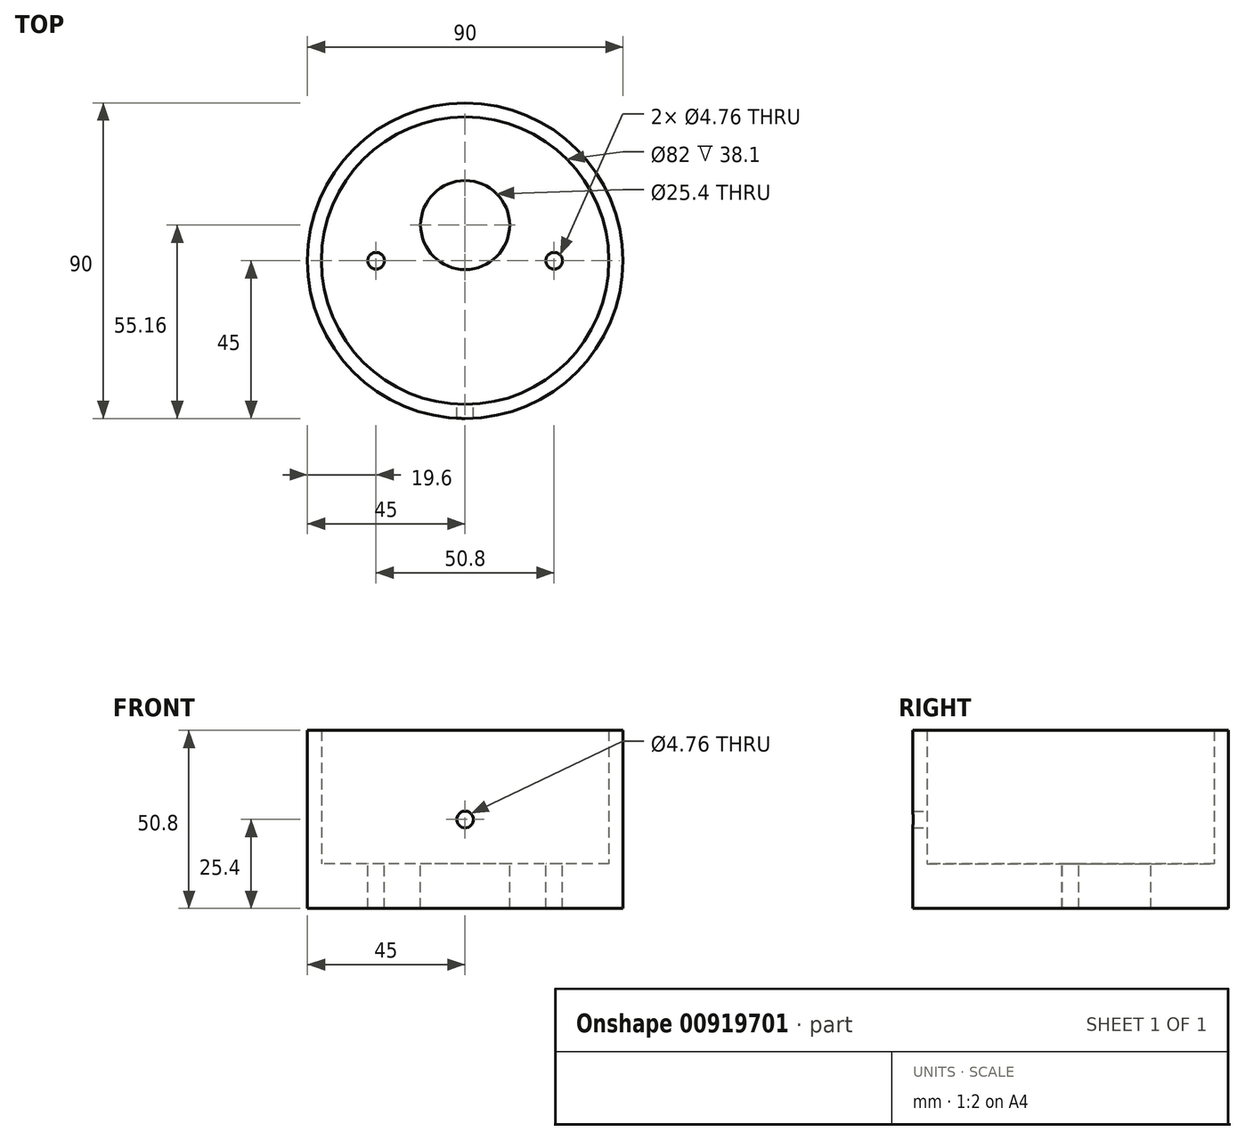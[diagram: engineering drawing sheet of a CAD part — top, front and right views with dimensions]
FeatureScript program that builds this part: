
annotation { "Feature Type Name" : "Feature", "Feature Type Description" : "" }
export const myFeature = defineFeature(function(context is Context, id is Id, definition is map)
    precondition{}
    {
        {
            var Q0;
            Q0=qCreatedBy(makeId("Top.planeOp"),FACE);
            var sketch = newSketch(context, id + "F0", { "sketchPlane" : qUnion([Q0])});
            skCircle(sketch, "E0", {"center": v(0, 0) * mm, "radius": 45 * mm});
            skSolve(sketch);
        }
        {
            var Q0;
            Q0 = qSketchRegion(id + "F0", true);
            extrude(context, id + "F1", {"entities" : qUnion([Q0]), "depth" : 12.7 * mm, "offsetDistance" : 25.4 * mm});
        }
        {
            var Q0;
            Q0=makeQuery(id+"F1.opExtrude","CAP_FACE",FACE,{"disambiguationData":[OSD([sQuery(id+"F0.wireOp",EDGE,"E0")])],"isStart":false});
            var sketch = newSketch(context, id + "F2", { "sketchPlane" : qUnion([Q0])});
            skCircle(sketch, "E1.0", {"center": v(0, 0) * mm, "radius": 45 * mm});
            skCircle(sketch, "E2", {"center": v(0, 0) * mm, "radius": 41 * mm});
            skSolve(sketch);
        }
        {
            var Q0;
            Q0 = qSketchRegion(id + "F2", true);
            extrude(context, id + "F3", {"entities" : qUnion([Q0]), "operationType" : NewBodyOperationType.ADD, "depth" : 38.1 * mm, "offsetDistance" : 25.4 * mm});
        }
        {
            var Q0;
            Q0=qCreatedBy(makeId("Front.planeOp"),FACE);
            var sketch = newSketch(context, id + "F4", { "sketchPlane" : qUnion([Q0])});
            skCircle(sketch, "E3", {"center": v(0, 25.4) * mm, "radius": 2.38 * mm});
            skSolve(sketch);
        }
        {
            var Q0;
            Q0 = qSketchRegion(id + "F4", true);
            extrude(context, id + "F5", {"entities" : qUnion([Q0]), "operationType" : NewBodyOperationType.REMOVE, "depth" : 79.5 * mm, "offsetDistance" : 25.4 * mm});
        }
        {
            var Q0;
            Q0=makeQuery(id+"F1.opExtrude","CAP_FACE",FACE,{"disambiguationData":[OSD([sQuery(id+"F0.wireOp",EDGE,"E0")])],"isStart":false});
            var sketch = newSketch(context, id + "F6", { "sketchPlane" : qUnion([Q0])});
            skCircle(sketch, "E4", {"center": v(-25.4, 0) * mm, "radius": 2.38 * mm});
            skCircle(sketch, "E5", {"center": v(25.4, 0) * mm, "radius": 2.38 * mm});
            skLineSegment(sketch, "E6", {"start": v(-25.4, 0) * mm, "end": v(25.4, 0) * mm, "construction": true});
            skSolve(sketch);
        }
        {
            var Q0;
            Q0 = qSketchRegion(id + "F6", true);
            extrude(context, id + "F7", {"entities" : qUnion([Q0]), "operationType" : NewBodyOperationType.REMOVE, "oppositeDirection" : true, "depth" : 25.4 * mm, "offsetDistance" : 25.4 * mm});
        }
        {
            var Q0;
            Q0=makeQuery(id+"F1.opExtrude","CAP_FACE",FACE,{"disambiguationData":[OSD([sQuery(id+"F0.wireOp",EDGE,"E0")])],"isStart":false});
            var sketch = newSketch(context, id + "F8", { "sketchPlane" : qUnion([Q0])});
            skCircle(sketch, "E7", {"center": v(0, 10.16) * mm, "radius": 12.7 * mm});
            skSolve(sketch);
        }
        {
            var Q0;
            Q0 = qSketchRegion(id + "F8", true);
            extrude(context, id + "F9", {"entities" : qUnion([Q0]), "operationType" : NewBodyOperationType.REMOVE, "oppositeDirection" : true, "depth" : 25.4 * mm, "offsetDistance" : 25.4 * mm});
        }
    });
